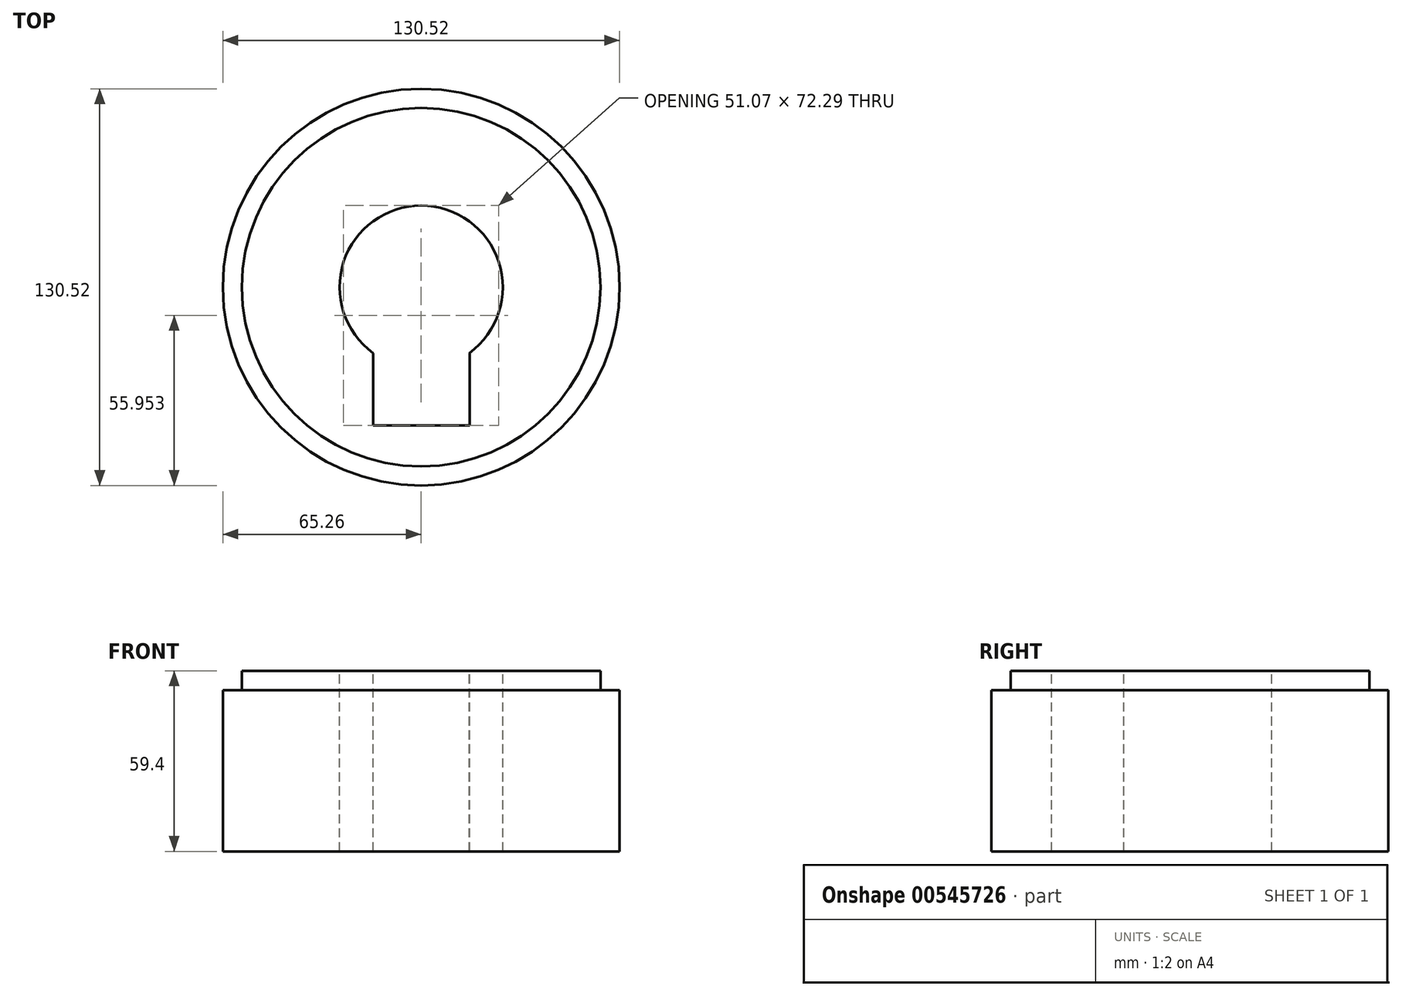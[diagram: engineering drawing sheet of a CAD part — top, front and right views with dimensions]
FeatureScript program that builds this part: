
annotation { "Feature Type Name" : "Feature", "Feature Type Description" : "" }
export const myFeature = defineFeature(function(context is Context, id is Id, definition is map)
    precondition{}
    {
        {
            var Q0;
            Q0=qCreatedBy(makeId("Top.planeOp"),FACE);
            var sketch = newSketch(context, id + "F0", { "sketchPlane" : qUnion([Q0])});
            skCircle(sketch, "E0", {"center": v(0, 0) * mm, "radius": 65.26 * mm});
            skSolve(sketch);
        }
        {
            var Q0;
            Q0 = qSketchRegion(id + "F0", true);
            extrude(context, id + "F1", {"entities" : qUnion([Q0]), "depth" : 53 * mm, "offsetDistance" : 25 * mm});
        }
        {
            var Q0;
            Q0=makeQuery(id+"F1.opExtrude","CAP_FACE",FACE,{"disambiguationData":[OSD([sQuery(id+"F0.wireOp",EDGE,"E0")])],"isStart":false});
            var sketch = newSketch(context, id + "F2", { "sketchPlane" : qUnion([Q0])});
            skCircle(sketch, "E1", {"center": v(0, 0) * mm, "radius": 58.97 * mm});
            skSolve(sketch);
        }
        {
            var Q0;
            Q0 = qSketchRegion(id + "F2", true);
            extrude(context, id + "F3", {"entities" : qUnion([Q0]), "operationType" : NewBodyOperationType.ADD, "depth" : 6.4 * mm, "offsetDistance" : 25 * mm});
        }
        {
            var Q0;
            Q0=makeQuery(id+"F3.opExtrude","CAP_FACE",FACE,{"disambiguationData":[OSD([sQuery(id+"F2.wireOp",EDGE,"E1")])],"isStart":false});
            var sketch = newSketch(context, id + "F4", { "sketchPlane" : qUnion([Q0])});
            skArc(sketch, "E2", {"start": v(15.8, -21.69) * mm, "mid": v(0, 26.84) * mm, "end": v(-15.8, -21.69) * mm});
            skLineSegment(sketch, "E3.bottom", {"start": v(15.8, -21.69) * mm, "end": v(15.89, -21.69) * mm});
            skLineSegment(sketch, "E3.top", {"start": v(-15.8, -45.45) * mm, "end": v(15.89, -45.45) * mm});
            skLineSegment(sketch, "E3.left", {"start": v(-15.8, -21.69) * mm, "end": v(-15.8, -45.45) * mm});
            skLineSegment(sketch, "E3.right", {"start": v(15.89, -21.69) * mm, "end": v(15.89, -45.45) * mm});
            skSolve(sketch);
        }
        {
            var Q0;
            Q0 = qSketchRegion(id + "F4", true);
            extrude(context, id + "F5", {"entities" : qUnion([Q0]), "operationType" : NewBodyOperationType.REMOVE, "oppositeDirection" : true, "depth" : 73.5 * mm, "offsetDistance" : 25 * mm});
        }
    });
